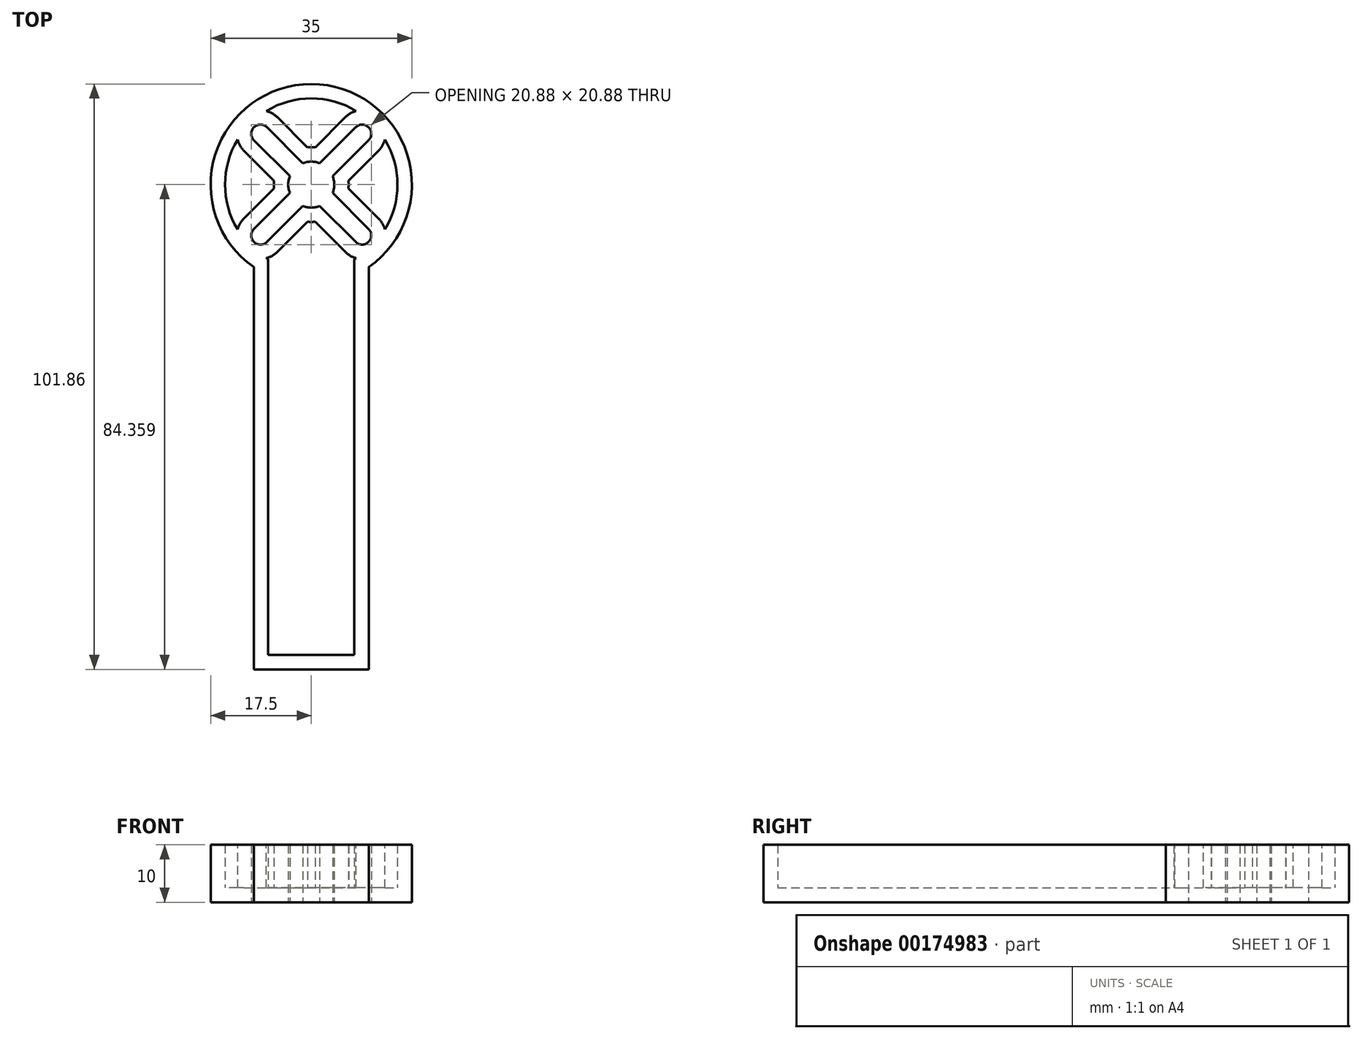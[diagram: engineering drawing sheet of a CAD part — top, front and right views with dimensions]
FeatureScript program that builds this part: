
annotation { "Feature Type Name" : "Feature", "Feature Type Description" : "" }
export const myFeature = defineFeature(function(context is Context, id is Id, definition is map)
    precondition{}
    {
        {
            assignVariable(context, id + "F0", {"name" : "armHeight", "anyValue" : 10});
        }
        {
            var Q0;
            Q0=qCreatedBy(makeId("Top.planeOp"),FACE);
            var sketch = newSketch(context, id + "F1", { "sketchPlane" : qUnion([Q0])});
            skLineSegment(sketch, "E0", {"start": v(-10, -50.3) * mm, "end": v(-10, 19.7) * mm});
            skLineSegment(sketch, "E1", {"start": v(10, -50.3) * mm, "end": v(10, 19.7) * mm});
            skLineSegment(sketch, "E2", {"start": v(-10, -50.3) * mm, "end": v(10, -50.3) * mm});
            skPoint(sketch, "E3", {"position": v(0, -50.3) * mm});
            skLineSegment(sketch, "E4", {"start": v(-10, -50.3) * mm, "end": v(0, -50.3) * mm});
            skLineSegment(sketch, "E5", {"start": v(10, -50.3) * mm, "end": v(0, -50.3) * mm});
            skCircle(sketch, "E6", {"center": v(0, 34.07) * mm, "radius": 17.5 * mm});
            skCircle(sketch, "E7", {"center": v(0, 34.07) * mm, "radius": 4 * mm});
            skLineSegment(sketch, "E8", {"start": v(0, 34.07) * mm, "end": v(8.84, 42.9) * mm, "construction": true});
            skLineSegment(sketch, "E9", {"start": v(0, 34.07) * mm, "end": v(-8.84, 25.23) * mm, "construction": true});
            skLineSegment(sketch, "E10", {"start": v(0, 34.07) * mm, "end": v(-8.84, 42.9) * mm, "construction": true});
            skLineSegment(sketch, "E11", {"start": v(0, 34.07) * mm, "end": v(8.84, 25.23) * mm, "construction": true});
            skCircle(sketch, "E12", {"center": v(-8.84, 42.9) * mm, "radius": 1.6 * mm});
            skCircle(sketch, "E13", {"center": v(-8.84, 25.23) * mm, "radius": 1.6 * mm});
            skCircle(sketch, "E14", {"center": v(8.84, 25.23) * mm, "radius": 1.6 * mm});
            skCircle(sketch, "E15", {"center": v(8.84, 42.9) * mm, "radius": 1.6 * mm});
            skLineSegment(sketch, "E16", {"start": v(-8.84, 25.23) * mm, "end": v(-9.97, 26.36) * mm});
            skLineSegment(sketch, "E17", {"start": v(-9.97, 26.36) * mm, "end": v(-3.72, 32.6) * mm});
            skLineSegment(sketch, "E18", {"start": v(-8.84, 25.23) * mm, "end": v(-7.7, 24.1) * mm});
            skLineSegment(sketch, "E19", {"start": v(-7.7, 24.1) * mm, "end": v(-1.46, 30.35) * mm});
            skLineSegment(sketch, "E20", {"start": v(8.84, 25.23) * mm, "end": v(7.7, 24.1) * mm});
            skLineSegment(sketch, "E21", {"start": v(7.7, 24.1) * mm, "end": v(1.46, 30.35) * mm});
            skLineSegment(sketch, "E22", {"start": v(8.84, 25.23) * mm, "end": v(9.97, 26.36) * mm});
            skLineSegment(sketch, "E23", {"start": v(9.97, 26.36) * mm, "end": v(3.72, 32.6) * mm});
            skLineSegment(sketch, "E24", {"start": v(-8.84, 42.9) * mm, "end": v(-9.97, 41.78) * mm});
            skLineSegment(sketch, "E25", {"start": v(-9.97, 41.78) * mm, "end": v(-3.72, 35.53) * mm});
            skLineSegment(sketch, "E26", {"start": v(-8.84, 42.9) * mm, "end": v(-7.7, 44.04) * mm});
            skLineSegment(sketch, "E27", {"start": v(-7.7, 44.04) * mm, "end": v(-1.46, 37.8) * mm});
            skLineSegment(sketch, "E28", {"start": v(9.97, 41.78) * mm, "end": v(8.84, 42.9) * mm});
            skLineSegment(sketch, "E29", {"start": v(9.97, 41.78) * mm, "end": v(3.72, 35.53) * mm});
            skLineSegment(sketch, "E30", {"start": v(8.84, 42.9) * mm, "end": v(9.97, 41.78) * mm});
            skLineSegment(sketch, "E31", {"start": v(8.84, 42.9) * mm, "end": v(7.7, 44.04) * mm});
            skLineSegment(sketch, "E32", {"start": v(7.7, 44.04) * mm, "end": v(1.46, 37.8) * mm});
            skLineSegment(sketch, "E33", {"start": v(0, -50.3) * mm, "end": v(0, 16.57) * mm, "construction": true});
            skSolve(sketch);
        }
        {
            var Q0;
            {var subQ1=sQuery(id+"F1.wireOp",EDGE,"E0");Q0=makeQuery(id+"F1.imprint","IMPRINT",FACE,{"disambiguationData":[TD([[makeQuery(id+"F1.imprint","IMPRINT",EDGE,{"derivedFrom":subQ1}),-1.0]])]});}
            var Q1;
            {var subQ14=sQuery(id+"F1.wireOp",EDGE,"E17");Q1=makeQuery(id+"F1.imprint","IMPRINT",FACE,{"disambiguationData":[TD([[makeQuery(id+"F1.imprint","IMPRINT",EDGE,{"derivedFrom":subQ14}),1.0]])]});}
            extrude(context, id + "F2", {"entities" : qUnion([Q0, Q1]), "depth" : (getVariable(context, 'armHeight')) * mm});
        }
        {
            var Q0;
            Q0=makeQuery(id+"F2.opExtrude","CAP_FACE",FACE,{"disambiguationData":[OSD([sQuery(id+"F1.wireOp",EDGE,"E0"),sQuery(id+"F1.wireOp",EDGE,"E1"),sQuery(id+"F1.wireOp",EDGE,"E4"),sQuery(id+"F1.wireOp",EDGE,"E5"),sQuery(id+"F1.wireOp",EDGE,"E6"),sQuery(id+"F1.wireOp",EDGE,"E7"),sQuery(id+"F1.wireOp",EDGE,"E12"),sQuery(id+"F1.wireOp",EDGE,"E13"),sQuery(id+"F1.wireOp",EDGE,"E14"),sQuery(id+"F1.wireOp",EDGE,"E15"),sQuery(id+"F1.wireOp",EDGE,"E17"),sQuery(id+"F1.wireOp",EDGE,"E19"),sQuery(id+"F1.wireOp",EDGE,"E21"),sQuery(id+"F1.wireOp",EDGE,"E23"),sQuery(id+"F1.wireOp",EDGE,"E25"),sQuery(id+"F1.wireOp",EDGE,"E27"),sQuery(id+"F1.wireOp",EDGE,"E29"),sQuery(id+"F1.wireOp",EDGE,"E32")])],"isStart":false});
            shell(context, id + "F3", {"entities" : qUnion([Q0]), "thickness" : 2.5 * mm});
        }
    });
